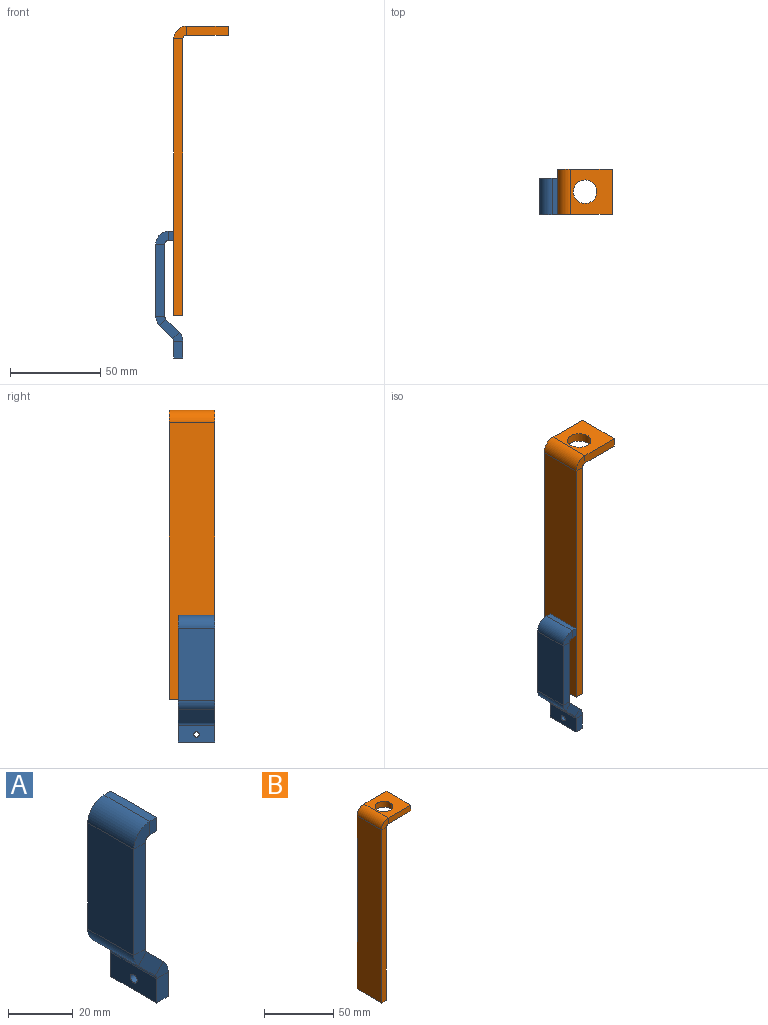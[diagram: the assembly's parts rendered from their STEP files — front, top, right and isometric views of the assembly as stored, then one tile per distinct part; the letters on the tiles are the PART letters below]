
ASSEMBLY  parts=2 mates=1
PART A: 31 faces, bbox 15x20x70 mm
  f0: plane 5x3mm, normal (0,1,0), area 15mm2, adj f2,f3,f4,f28
  f1: plane 5x3mm, normal (0,-1,0), area 15mm2, adj f2,f3,f4,f27
  f2: plane 20x5mm, normal (1,0,0), area 100mm2, adj f0,f1,f3,f4
  f3: plane 20x3mm, normal (0,0,1), area 60mm2, adj f0,f1,f2,f29
  f4: plane 20x3mm, normal (0,0,-1), area 60mm2, adj f0,f1,f2,f30
  f5: plane 40.1x5mm, normal (0,1,0), area 200.5mm2, adj f7,f8,f24,f28
  f6: plane 40.1x5mm, normal (0,-1,0), area 200.5mm2, adj f7,f8,f23,f27
  f7: plane 40.1x20mm, normal (-1,0,0), area 802mm2, adj f5,f6,f25,f29
  f8: plane 40.1x20mm, normal (1,0,0), area 802mm2, adj f5,f6,f26,f30
  f9: plane 10.9x10.9mm, normal (0,1,0), area 52.1mm2, adj f11,f12,f20,f24
  f10: plane 10.9x10.9mm, normal (0,-1,0), area 52.1mm2, adj f11,f12,f19,f23
  f11: plane 20x7.36mm, normal (-0.71,0,-0.71), area 208.3mm2, adj f9,f10,f22,f25
  f12: plane 20x7.36mm, normal (0.71,0,0.71), area 208.3mm2, adj f9,f10,f21,f26
  f13: plane 9.17x5mm, normal (0,1,0), area 45.9mm2, adj f14,f17,f18,f20
  f14: plane 20x5mm, normal (0,0,-1), area 100mm2, adj f13,f15,f17,f18
  f15: plane 9.17x5mm, normal (0,-1,0), area 45.9mm2, adj f14,f17,f18,f19
  f16: cylinder r=1.5mm len=5mm, axis (-1,0,0), area 47.1mm2, adj f17,f18
  f17: plane 20x9.17mm, normal (-1,0,0), area 176.4mm2, adj f13,f14,f15,f16,f22
  f18: plane 20x9.17mm, normal (1,0,0), area 176.4mm2, adj f13,f14,f15,f16,f21
  f19: plane 5.59x4.95mm, normal (0,-1,0), area 17.7mm2, adj f10,f15,f21,f22
  f20: plane 5.59x4.95mm, normal (0,1,0), area 17.7mm2, adj f9,f13,f21,f22
  f21: cylinder r=7mm len=20mm, axis (0,-1,0), area 110mm2, adj f12,f18,f19,f20
  f22: cylinder r=2mm len=20mm, axis (0,-1,0), area 31.4mm2, adj f11,f17,f19,f20
  f23: plane 5.59x4.95mm, normal (0,-1,0), area 17.7mm2, adj f6,f10,f25,f26
  f24: plane 5.59x4.95mm, normal (0,1,0), area 17.7mm2, adj f5,f9,f25,f26
  f25: cylinder r=7mm len=20mm, axis (0,-1,0), area 110mm2, adj f7,f11,f23,f24
  f26: cylinder r=2mm len=20mm, axis (0,-1,0), area 31.4mm2, adj f8,f12,f23,f24
  f27: plane 7x7mm, normal (0,-1,0), area 35.3mm2, adj f1,f6,f29,f30
  f28: plane 7x7mm, normal (0,1,0), area 35.3mm2, adj f0,f5,f29,f30
  f29: cylinder r=7mm len=20mm, axis (0,-1,0), area 219.9mm2, adj f3,f7,f27,f28
  f30: cylinder r=2mm len=20mm, axis (0,-1,0), area 62.8mm2, adj f4,f8,f27,f28
PART B: 15 faces, bbox 30x25x160 mm
  f0: plane 153x5mm, normal (0,1,0), area 765mm2, adj f1,f3,f4,f12
  f1: plane 25x5mm, normal (0,0,-1), area 125mm2, adj f0,f2,f3,f4
  f2: plane 153x5mm, normal (0,-1,0), area 765mm2, adj f1,f3,f4,f11
  f3: plane 153x25mm, normal (-1,0,0), area 3825mm2, adj f0,f1,f2,f13
  f4: plane 153x25mm, normal (1,0,0), area 3825mm2, adj f0,f1,f2,f14
  f5: plane 23x5mm, normal (0,1,0), area 115mm2, adj f8,f9,f10,f12
  f6: plane 23x5mm, normal (0,-1,0), area 115mm2, adj f8,f9,f10,f11
  f7: cylinder r=6.5mm len=13mm, axis (0,0,1), area 204.2mm2, adj f9,f10
  f8: plane 25x5mm, normal (1,0,0), area 125mm2, adj f5,f6,f9,f10
  f9: plane 25x23mm, normal (0,0,1), area 442.3mm2, adj f5,f6,f7,f8,f13
  f10: plane 25x23mm, normal (0,0,-1), area 442.3mm2, adj f5,f6,f7,f8,f14
  f11: plane 7x7mm, normal (0,-1,0), area 35.3mm2, adj f2,f6,f13,f14
  f12: plane 7x7mm, normal (0,1,0), area 35.3mm2, adj f0,f5,f13,f14
  f13: cylinder r=7mm len=25mm, axis (0,-1,0), area 274.9mm2, adj f3,f9,f11,f12
  f14: cylinder r=2mm len=25mm, axis (0,-1,0), area 78.5mm2, adj f4,f10,f11,f12
PLACE A t=(-32.44,-32.75,-96.08)mm
PLACE B t=(-22.44,-27.75,17.42)mm
MATE fastened A.f2 <-> B.f3  axis (1,0,0) through (-22.44,-52.75,-96.08)mm
